# Revit family: PRD_FrankeWS_HndDrrs_EXOSElectronicHandDryer_EXOS220X_220B_220W
name_source: partatom
category: Specialty Equipment
revit_build: Autodesk Revit 2018 (Build: 20190510_1515(x64)
units: mm (PartAtom-declared; Revit-internal decimal feet)

## family parameters
Cut with Voids When Loaded = No
Host = Face
OmniClass Number = 23.40.20.21.14
OmniClass Title = Hand and Hair Dryers
Part Type = Normal
Room Calculation Point = No
Round Connector Dimension = Use Diameter
Shared = No

## types (3) — shared parameters
AirVelocity = Adjustable, 95-115 m/s
AirVolume = 80 m3/h
ApparentLoad = 0 VA
AssetType = Fixed
Category = Pr_40_70_62_37, Hand dryers
ConnectionVoltage = 230 V, 50-60 Hz
Default Elevation = 1200 mm
DispenserMaterial = PRD_AR_StainlessSteel_SatinFinished
DurationUnit = year
Features = Stainless steel, surface satin finished
Finish = satin finished
HeatingPower = 500.00 watt
IP_Code = IPX1
IfcExportAs = IfcElectricApplianceType
IfcExportType = HANDDRYER
InputSupplyVoltageHz = 50.00 hertz
InputSupplyVoltageV = 220.00 volt
IntegralAccessories = cable and plug not included
LoadClassification = Other
Manufacturer = KWC Group AG
ManufacturerName = KWC Group AG
ManufacturerURL = www.kwc.com
Material = Stainless steel
MaterialCode = 1.4301
MaterialThickness = 1.20 mm
MotorPower = 500.00 watt
NBSDescription = Hand dryers
NBSReference = 45-35-72/334
NominalDepth = 120 mm  [stored 0.393701 ft]
NominalFrequencyRange = 50-60 Hz
NominalHeight = 325 mm  [stored 1.06627 ft]
NominalWidth = 200 mm  [stored 0.656168 ft]
PowerFactor = 1
ProductInformation = https://pim.kwc.com
ProtectiveSystemIP = IPX1
RatedCurrent = 0
RatedVoltage = 230 V
Size = 200 x 325 x 120 mm
SoundLevel = 76.20 dB
SurfaceTreatment = InoxPlus (anti fingerprint)
TotalPower = 1,000.00 watt
TypeOfFixing = Screw
TypeOfMounting = Wall mounting
TypeOfOperation = Sensor operation
URL = www.kwc.com
Uniclass2015Code = Pr_40_70_62_37
Uniclass2015Title = Hand dryers
Uniclass2015Version = Products v1.17
Version = 1
Voltage = 230 V
WarrantyDurationUnit = year

## per-type parameters (varying)
| type | BIMObjectName | Description | GrossWeight | ModelNumber | Name | NetWeight | PanelMaterial |
| EXOS220X | PRD_AR_HndDrrs_EXOSElectronicHandDryer_EXOS220X | Hand dryer for wall mounting, stainless steel with satin-finish and InoxPlus surface refinement for the reduction of finger marks and better cleaning characteristics (easy to clean), material thickness 1.2 mm, with contactless opto-electronic sensor for touch-free operation, adjustable hot air temperature, sensor range adjustable from 10 to 25 cm, protection from continuous operation with automatic switch-off after 60 seconds, air speed adjustable, cable and plug not included. | 5.42 kg | 2030027981 | EXOS Electronic Hand Dryer EXOS220X | 4.35 kg | PRD_AR_StainlessSteel_SatinFinished |
| EXOS220B | PRD_AR_HndDrrs_EXOSElectronicHandDryer_EXOS220B | Hand dryer for wall mounting, stainless steel with satin-finish, black safety glass front panel and casing with InoxPlus surface refinement for the reduction of finger marks and better cleaning characteristics (easy to clean), material thickness 1.2 mm, with contactless opto-electronic sensor for touch-free operation, adjustable hot air temperature, sensor range adjustable from 10 to 25 cm, protection from continuous operation with automatic switch-off after 60 seconds, air speed adjustable, cable and plug not included. | 6.07 kg | 2030034622 | EXOS Electronic Hand Dryer EXOS220B | 4.92 kg | PRD_AR_Glass_Black |
| EXOS220W | PRD_AR_HndDrrs_EXOSElectronicHandDryer_EXOS220W | Hand dryer for wall mounting, stainless steel with satin-finish, white safety glass front panel and casing with InoxPlus surface refinement for the reduction of finger marks and better cleaning characteristics (easy to clean), material thickness 1.2 mm, with contactless opto-electronic sensor for touch-free operation, adjustable hot air temperature, sensor range adjustable from 10 to 25 cm, protection from continuous operation with automatic switch-off after 60 seconds, air speed adjustable, cable and plug not included. | 6.07 kg | 2030034660 | EXOS Electronic Hand Dryer EXOS220W | 4.92 kg | PRD_AR_Glass_White |

note: column(s) folded — value = type name in every type: Model, ModelReference

note: [stored X ft] marks values corroborated as IEEE doubles in the binary element streams (Revit-internal decimal feet)

## geometry (parser evidence)
native form markers: Sweep x4
no freeform markers — native parametric forms only
